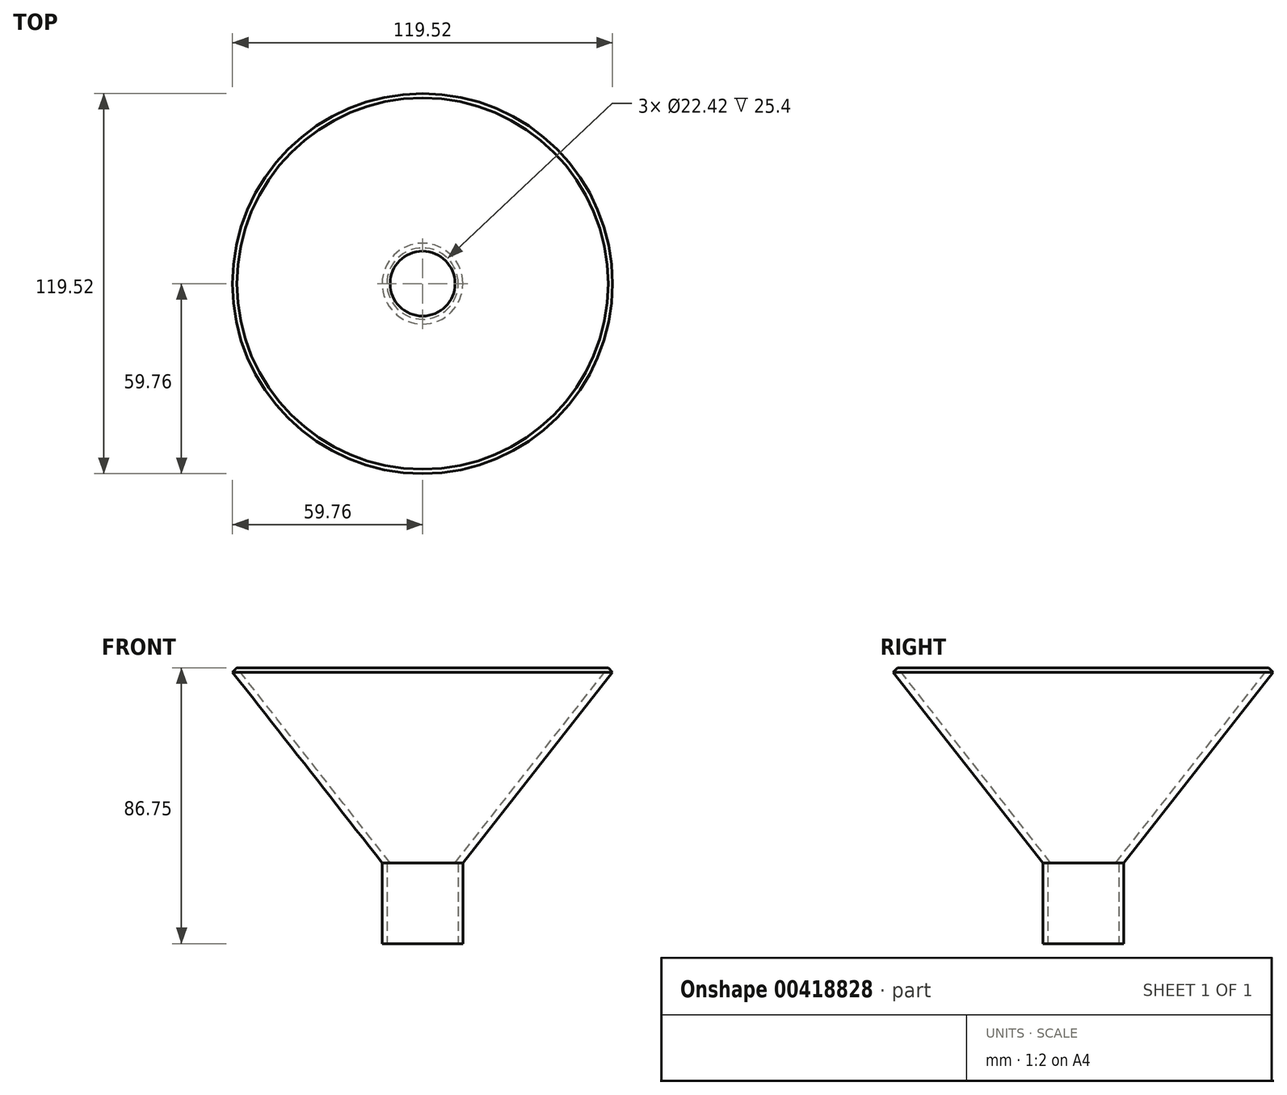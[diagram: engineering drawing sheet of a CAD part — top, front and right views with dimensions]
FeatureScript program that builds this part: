
annotation { "Feature Type Name" : "Feature", "Feature Type Description" : "" }
export const myFeature = defineFeature(function(context is Context, id is Id, definition is map)
    precondition{}
    {
        {
            var Q0;
            Q0=qCreatedBy(makeId("Front.planeOp"),FACE);
            var sketch = newSketch(context, id + "F0", { "sketchPlane" : qUnion([Q0])});
            skLineSegment(sketch, "E0", {"start": v(0, 0) * mm, "end": v(47.06, 59.93) * mm});
            skLineSegment(sketch, "E1", {"start": v(0, 0) * mm, "end": v(0, -25.4) * mm});
            skLineSegment(sketch, "E2", {"start": v(0, -25.4) * mm, "end": v(-12.7, -25.4) * mm});
            skLineSegment(sketch, "E3", {"start": v(-12.7, -25.4) * mm, "end": v(-12.7, 0) * mm});
            skLineSegment(sketch, "E4", {"start": v(-12.7, 0) * mm, "end": v(-2.5, 0) * mm});
            skLineSegment(sketch, "E5", {"start": v(-2.5, 0) * mm, "end": v(45.67, 61.35) * mm});
            skLineSegment(sketch, "E6", {"start": v(45.67, 61.35) * mm, "end": v(47.06, 59.93) * mm});
            skSolve(sketch);
        }
        {
            var Q0;
            Q0 = qSketchRegion(id + "F0", true);
            var Q1;
            Q1=sQuery(id+"F0.wireOp",EDGE,"E3");
            revolve(context, id + "F1", {"entities" : qUnion([Q0]), "axis" : qUnion([Q1]), "revolveType" : RevolveType.FULL});
        }
        {
            var Q0;
            Q0=makeQuery(id+"F1.opRevolve","SWEPT_FACE",FACE,{"disambiguationData":[OSD([sQuery(id+"F0.wireOp",EDGE,"E2")])]});
            var sketch = newSketch(context, id + "F2", { "sketchPlane" : qUnion([Q0])});
            skCircle(sketch, "E7", {"center": v(-12.7, 0) * mm, "radius": 11.2 * mm});
            skSolve(sketch);
        }
        {
            var Q0;
            Q0=makeQuery(id+"F2.imprint","IMPRINT",FACE,{"disambiguationData":[TD([[makeQuery(id+"F2.imprint","IMPRINT",EDGE,{"derivedFrom":sQuery(id+"F2.wireOp",EDGE,"E7")}),1.0]])]});
            extrude(context, id + "F3", {"entities" : qUnion([Q0]), "operationType" : NewBodyOperationType.REMOVE, "oppositeDirection" : true, "depth" : 25.4 * mm});
        }
    });
